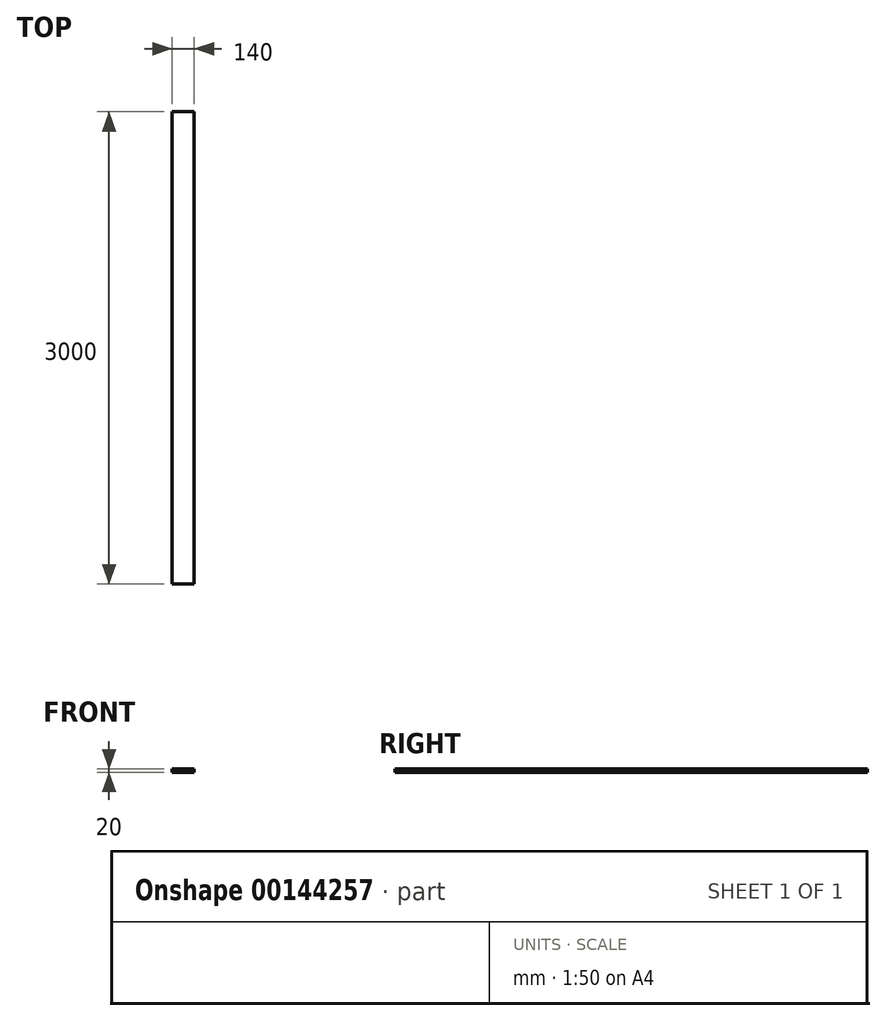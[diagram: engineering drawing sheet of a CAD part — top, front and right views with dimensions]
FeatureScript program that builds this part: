
annotation { "Feature Type Name" : "Feature", "Feature Type Description" : "" }
export const myFeature = defineFeature(function(context is Context, id is Id, definition is map)
    precondition{}
    {
        {
            var Q0;
            Q0=qCreatedBy(makeId("Front.planeOp"),FACE);
            var sketch = newSketch(context, id + "F0", { "sketchPlane" : qUnion([Q0])});
            skLineSegment(sketch, "E0.bottom", {"start": v(0, 0) * mm, "end": v(140, 0) * mm});
            skLineSegment(sketch, "E0.top", {"start": v(0, 20) * mm, "end": v(140, 20) * mm});
            skLineSegment(sketch, "E0.left", {"start": v(0, 0) * mm, "end": v(0, 20) * mm});
            skLineSegment(sketch, "E0.right", {"start": v(140, 0) * mm, "end": v(140, 20) * mm});
            skSolve(sketch);
        }
        {
            var Q0;
            Q0=makeQuery(id+"F0.imprint","IMPRINT",FACE,{"disambiguationData":[TD([[makeQuery(id+"F0.imprint","IMPRINT",EDGE,{"derivedFrom":sQuery(id+"F0.wireOp",EDGE,"E0.bottom")}),1.0]])]});
            extrude(context, id + "F1", {"entities" : qUnion([Q0]), "depth" : 3000 * mm});
        }
    });
